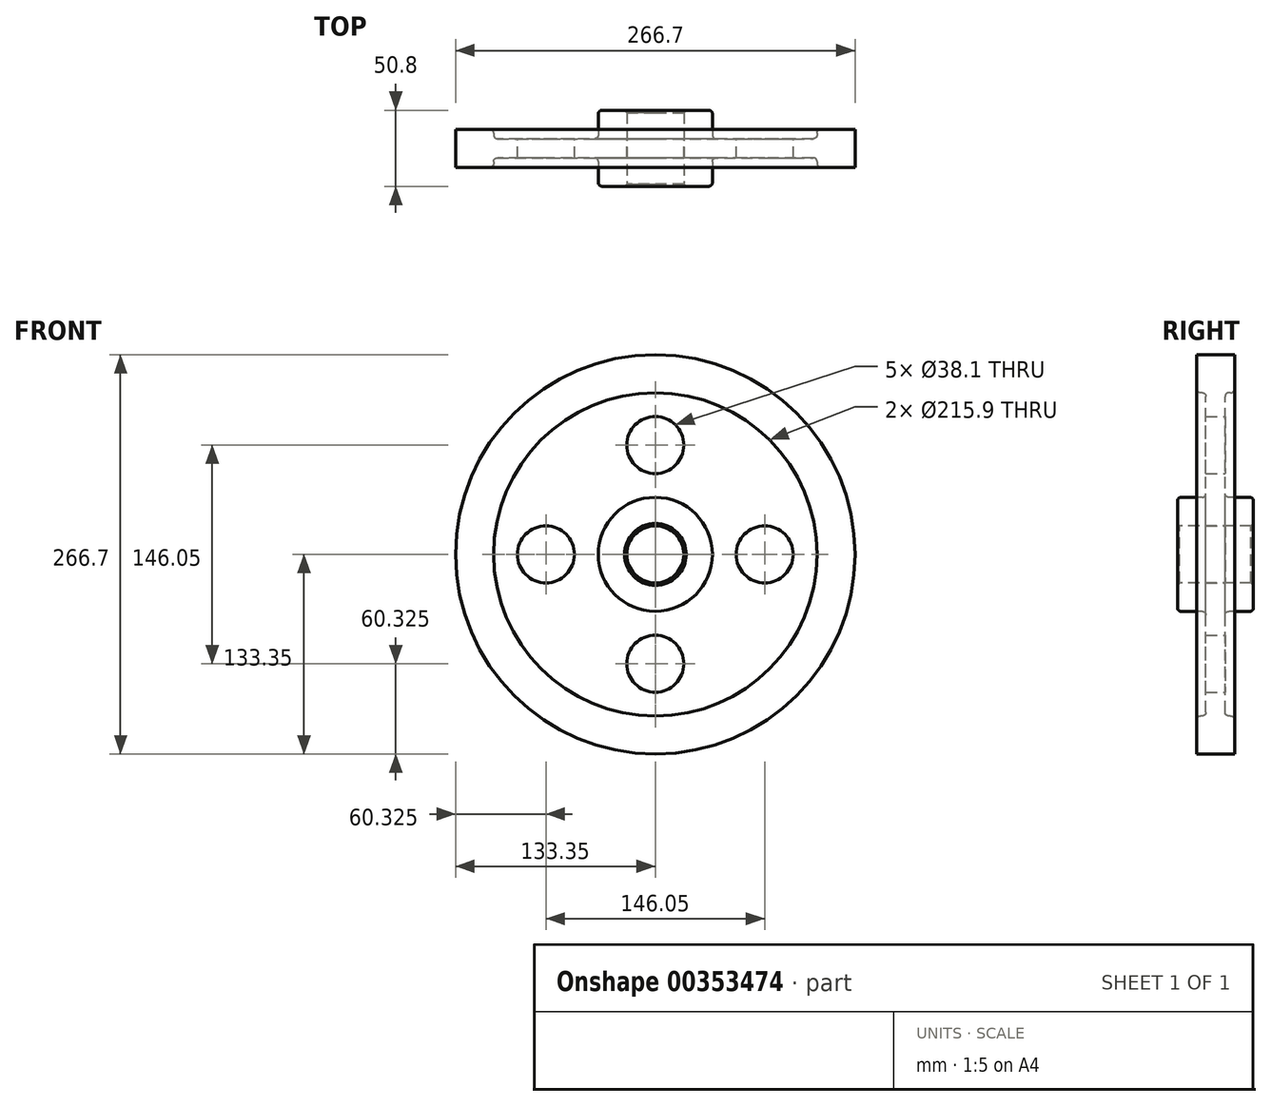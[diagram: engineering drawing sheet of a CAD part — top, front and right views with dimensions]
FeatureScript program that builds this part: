
annotation { "Feature Type Name" : "Feature", "Feature Type Description" : "" }
export const myFeature = defineFeature(function(context is Context, id is Id, definition is map)
    precondition{}
    {
        {
            var Q0;
            Q0=qCreatedBy(makeId("Right.planeOp"),FACE);
            var sketch = newSketch(context, id + "F0", { "sketchPlane" : qUnion([Q0])});
            skLineSegment(sketch, "E0", {"start": v(0, 0) * mm, "end": v(125.12, 0) * mm, "construction": true});
            skLineSegment(sketch, "E1.0", {"start": v(0, 19.05) * mm, "end": v(25.4, 19.05) * mm});
            skLineSegment(sketch, "E2.0", {"start": v(6.35, 38.1) * mm, "end": v(25.4, 38.1) * mm});
            skLineSegment(sketch, "E3.0", {"start": v(6.35, 107.95) * mm, "end": v(12.7, 107.95) * mm});
            skLineSegment(sketch, "E4.0", {"start": v(0, 133.35) * mm, "end": v(12.7, 133.35) * mm});
            skLineSegment(sketch, "E5", {"start": v(0, 0) * mm, "end": v(0, 133.35) * mm, "construction": true});
            skLineSegment(sketch, "E6.0", {"start": v(25.4, 19.05) * mm, "end": v(25.4, 38.1) * mm});
            skLineSegment(sketch, "E7.trimOffspring", {"start": v(12.7, 107.95) * mm, "end": v(12.7, 133.35) * mm});
            skLineSegment(sketch, "E8.trimOffspring", {"start": v(6.35, 38.1) * mm, "end": v(6.35, 107.95) * mm});
            skPoint(sketch, "E9.MirrorCS.end.orphan", {"position": v(12.7, 133.35) * mm});
            skPoint(sketch, "E10.MirrorP", {"position": v(-12.7, 133.35) * mm});
            skLineSegment(sketch, "E11.MirrorCS", {"start": v(-12.7, 107.95) * mm, "end": v(-12.7, 133.35) * mm});
            skLineSegment(sketch, "E12.MirrorCS", {"start": v(-6.35, 38.1) * mm, "end": v(-6.35, 107.95) * mm});
            skLineSegment(sketch, "E13.MirrorCS", {"start": v(-6.35, 38.1) * mm, "end": v(-25.4, 38.1) * mm});
            skLineSegment(sketch, "E14.MirrorCS", {"start": v(-25.4, 19.05) * mm, "end": v(-25.4, 38.1) * mm});
            skLineSegment(sketch, "E15.MirrorCS", {"start": v(0, 19.05) * mm, "end": v(-25.4, 19.05) * mm});
            skPoint(sketch, "E16.MirrorP", {"position": v(-6.35, 133.35) * mm});
            skLineSegment(sketch, "E17.MirrorCS", {"start": v(-6.35, 107.95) * mm, "end": v(-12.7, 107.95) * mm});
            skLineSegment(sketch, "E18.MirrorCS", {"start": v(0, 133.35) * mm, "end": v(-12.7, 133.35) * mm});
            skSolve(sketch);
        }
        {
            var Q0;
            Q0 = qSketchRegion(id + "F0", true);
            var Q1;
            Q1=sQuery(id+"F0.wireOp",EDGE,"E0");
            revolve(context, id + "F1", {"entities" : qUnion([Q0]), "axis" : qUnion([Q1]), "revolveType" : RevolveType.FULL});
        }
        {
            var Q0;
            Q0=makeQuery(id+"F1.opRevolve","SWEPT_FACE",FACE,{"disambiguationData":[OSD([sQuery(id+"F0.wireOp",EDGE,"E8.trimOffspring")])]});
            var sketch = newSketch(context, id + "F2", { "sketchPlane" : qUnion([Q0])});
            skPoint(sketch, "E19.start.orphan", {"position": v(0, 0) * mm});
            skLineSegment(sketch, "E20", {"start": v(0, 0) * mm, "end": v(0, 73.03) * mm});
            skCircle(sketch, "E21", {"center": v(0, 73.03) * mm, "radius": 19.05 * mm});
            skCircle(sketch, "E22.1.0", {"center": v(-73.03, 0) * mm, "radius": 19.05 * mm});
            skCircle(sketch, "E22.2.0", {"center": v(0, -73.03) * mm, "radius": 19.05 * mm});
            skCircle(sketch, "E22.3.0", {"center": v(73.03, 0) * mm, "radius": 19.05 * mm});
            skSolve(sketch);
        }
        {
            var Q0;
            Q0=makeQuery(id+"F2.imprint","IMPRINT",FACE,{"disambiguationData":[TD([[makeQuery(id+"F2.imprint","IMPRINT",EDGE,{"derivedFrom":sQuery(id+"F2.wireOp",EDGE,"E22.3.0")}),1.0]])]});
            var Q1;
            Q1=makeQuery(id+"F2.imprint","IMPRINT",FACE,{"disambiguationData":[TD([[makeQuery(id+"F2.imprint","IMPRINT",EDGE,{"derivedFrom":sQuery(id+"F2.wireOp",EDGE,"E22.1.0")}),1.0]])]});
            var Q2;
            Q2=makeQuery(id+"F2.imprint","IMPRINT",FACE,{"disambiguationData":[TD([[makeQuery(id+"F2.imprint","IMPRINT",EDGE,{"derivedFrom":sQuery(id+"F2.wireOp",EDGE,"E22.2.0")}),1.0]])]});
            var Q3;
            Q3=makeQuery(id+"F2.imprint","IMPRINT",FACE,{"disambiguationData":[TD([[makeQuery(id+"F2.imprint","IMPRINT",EDGE,{"derivedFrom":sQuery(id+"F2.wireOp",EDGE,"E21")}),1.0]])]});
            extrude(context, id + "F3", {"entities" : qUnion([Q0, Q1, Q2, Q3]), "operationType" : NewBodyOperationType.REMOVE, "oppositeDirection" : true, "depth" : 25.4 * mm});
        }
        {
            var Q0;
            Q0=makeQuery(id+"F1.opRevolve","SWEPT_EDGE",EDGE,{"disambiguationData":[OSD([sQuery(id+"F0.wireOp",EDGE,"E2.0"),sQuery(id+"F0.wireOp",EDGE,"E6.0")])]});
            var Q1;
            Q1=makeQuery(id+"F1.opRevolve","SWEPT_EDGE",EDGE,{"disambiguationData":[OSD([sQuery(id+"F0.wireOp",EDGE,"E2.0"),sQuery(id+"F0.wireOp",EDGE,"E8.trimOffspring")])]});
            var Q2;
            Q2=makeQuery(id+"F1.opRevolve","SWEPT_EDGE",EDGE,{"disambiguationData":[OSD([sQuery(id+"F0.wireOp",EDGE,"E3.0"),sQuery(id+"F0.wireOp",EDGE,"E7.trimOffspring")])]});
            var Q3;
            Q3=makeQuery(id+"F1.opRevolve","SWEPT_EDGE",EDGE,{"disambiguationData":[OSD([sQuery(id+"F0.wireOp",EDGE,"E3.0"),sQuery(id+"F0.wireOp",EDGE,"E8.trimOffspring")])]});
            fillet(context, id + "F4", {"entities" : qUnion([Q0, Q1, Q2, Q3]), "radius" : 2.54 * mm, "tangentPropagation" : true, "allowEdgeOverflow" : false});
        }
        {
            var Q0;
            Q0=makeQuery(id+"F1.opRevolve","SWEPT_EDGE",EDGE,{"disambiguationData":[OSD([sQuery(id+"F0.wireOp",EDGE,"E1.0"),sQuery(id+"F0.wireOp",EDGE,"E6.0")])]});
            var Q1;
            Q1=makeQuery(id+"F1.opRevolve","SWEPT_EDGE",EDGE,{"disambiguationData":[OSD([sQuery(id+"F0.wireOp",EDGE,"E14.MirrorCS"),sQuery(id+"F0.wireOp",EDGE,"E15.MirrorCS")])]});
            chamfer(context, id + "F5", {"entities" : qUnion([Q0, Q1]), "width" : 1.59 * mm, "tangentPropagation" : true});
        }
        {
            var Q0;
            Q0=makeQuery(id+"F1.opRevolve","SWEPT_EDGE",EDGE,{"disambiguationData":[OSD([sQuery(id+"F0.wireOp",EDGE,"E12.MirrorCS"),sQuery(id+"F0.wireOp",EDGE,"E17.MirrorCS")])]});
            var Q1;
            Q1=makeQuery(id+"F1.opRevolve","SWEPT_EDGE",EDGE,{"disambiguationData":[OSD([sQuery(id+"F0.wireOp",EDGE,"E11.MirrorCS"),sQuery(id+"F0.wireOp",EDGE,"E17.MirrorCS")])]});
            var Q2;
            Q2=makeQuery(id+"F1.opRevolve","SWEPT_EDGE",EDGE,{"disambiguationData":[OSD([sQuery(id+"F0.wireOp",EDGE,"E12.MirrorCS"),sQuery(id+"F0.wireOp",EDGE,"E13.MirrorCS")])]});
            var Q3;
            Q3=makeQuery(id+"F1.opRevolve","SWEPT_EDGE",EDGE,{"disambiguationData":[OSD([sQuery(id+"F0.wireOp",EDGE,"E13.MirrorCS"),sQuery(id+"F0.wireOp",EDGE,"E14.MirrorCS")])]});
            fillet(context, id + "F6", {"entities" : qUnion([Q0, Q1, Q2, Q3]), "radius" : 2.54 * mm, "tangentPropagation" : true, "allowEdgeOverflow" : false});
        }
    });
